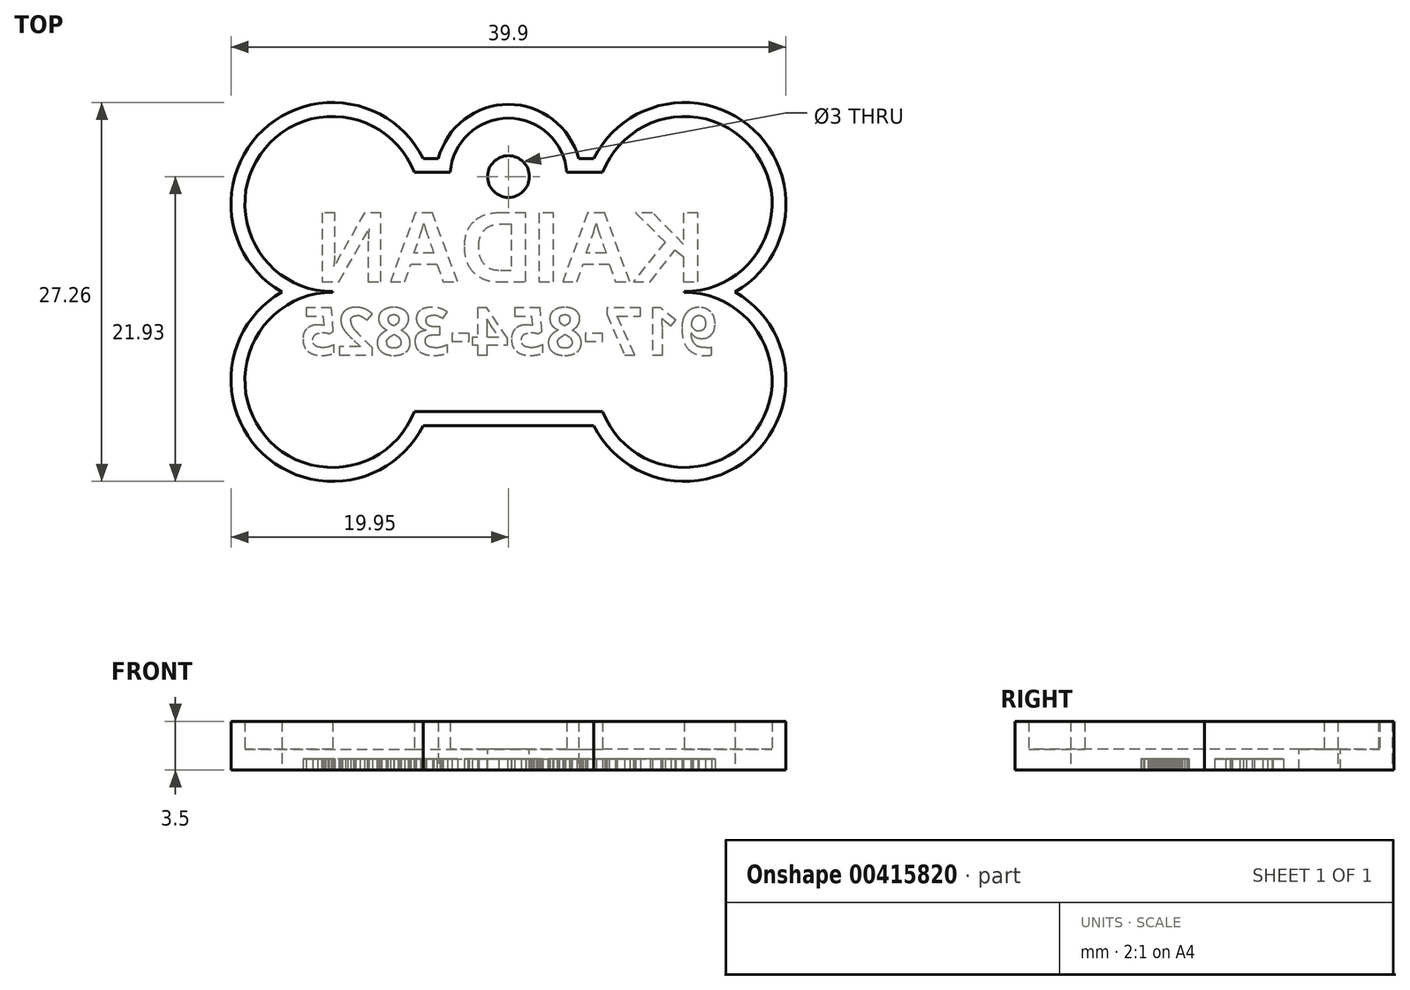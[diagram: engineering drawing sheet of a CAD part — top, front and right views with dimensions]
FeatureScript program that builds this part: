
annotation { "Feature Type Name" : "Feature", "Feature Type Description" : "" }
export const myFeature = defineFeature(function(context is Context, id is Id, definition is map)
    precondition{}
    {
        {
            var Q0;
            Q0=qCreatedBy(makeId("Top.planeOp"),FACE);
            var sketch = newSketch(context, id + "F0", { "sketchPlane" : qUnion([Q0])});
            skLineSegment(sketch, "E0.bottom", {"start": v(12.65, -6.32) * mm, "end": v(-12.65, -6.33) * mm, "construction": true});
            skLineSegment(sketch, "E0.top", {"start": v(12.65, 6.33) * mm, "end": v(-12.65, 6.32) * mm, "construction": true});
            skLineSegment(sketch, "E0.left", {"start": v(12.65, -6.32) * mm, "end": v(12.65, 6.33) * mm, "construction": true});
            skLineSegment(sketch, "E0.right", {"start": v(-12.65, -6.33) * mm, "end": v(-12.65, 6.32) * mm, "construction": true});
            skPoint(sketch, "E0.middle", {"position": v(0, 0) * mm});
            skArc(sketch, "E1", {"start": v(12.65, 0.03) * mm, "mid": v(17.85, 9.89) * mm, "end": v(6.78, 8.6) * mm});
            skArc(sketch, "E2", {"start": v(6.78, -8.6) * mm, "mid": v(17.85, -9.89) * mm, "end": v(12.65, -0.02) * mm});
            skArc(sketch, "E3", {"start": v(-12.65, -0.03) * mm, "mid": v(-17.85, -9.89) * mm, "end": v(-6.78, -8.6) * mm});
            skArc(sketch, "E4", {"start": v(-6.78, 8.6) * mm, "mid": v(-17.85, 9.89) * mm, "end": v(-12.65, 0.02) * mm});
            skLineSegment(sketch, "E5", {"start": v(-12.65, 0.02) * mm, "end": v(-12.65, -0.03) * mm});
            skLineSegment(sketch, "E6", {"start": v(12.65, -0.02) * mm, "end": v(12.65, 0.03) * mm});
            skLineSegment(sketch, "E7", {"start": v(-6.78, 8.6) * mm, "end": v(-4.19, 8.6) * mm});
            skLineSegment(sketch, "E8", {"start": v(-6.78, -8.6) * mm, "end": v(6.78, -8.6) * mm});
            skArc(sketch, "E9", {"start": v(4.19, 8.6) * mm, "mid": v(0, 12.5) * mm, "end": v(-4.19, 8.6) * mm});
            skPoint(sketch, "E10", {"position": v(0, 12.5) * mm});
            skCircle(sketch, "E11", {"center": v(0, 8.3) * mm, "radius": 1.5 * mm});
            skLineSegment(sketch, "E12.trimOffspring", {"start": v(4.19, 8.6) * mm, "end": v(6.78, 8.6) * mm});
            skLineSegment(sketch, "E13.0", {"start": v(-6.13, 9.6) * mm, "end": v(-5.03, 9.6) * mm});
            skArc(sketch, "E13.1", {"start": v(5.03, 9.6) * mm, "mid": v(0, 13.5) * mm, "end": v(-5.03, 9.6) * mm});
            skArc(sketch, "E13.2", {"start": v(-6.13, 9.6) * mm, "mid": v(-17.66, 11.63) * mm, "end": v(-16.3, 0) * mm});
            skLineSegment(sketch, "E13.3", {"start": v(5.03, 9.6) * mm, "end": v(6.13, 9.6) * mm});
            skArc(sketch, "E13.4", {"start": v(-16.3, 0) * mm, "mid": v(-17.66, -11.63) * mm, "end": v(-6.13, -9.6) * mm});
            skLineSegment(sketch, "E13.5", {"start": v(-6.13, -9.6) * mm, "end": v(6.13, -9.6) * mm});
            skArc(sketch, "E13.6", {"start": v(6.13, -9.6) * mm, "mid": v(17.66, -11.63) * mm, "end": v(16.3, 0) * mm});
            skArc(sketch, "E13.7", {"start": v(16.3, 0) * mm, "mid": v(17.66, 11.63) * mm, "end": v(6.13, 9.6) * mm});
            skSolve(sketch);
        }
        {
            var Q0;
            Q0=makeQuery(id+"F0.imprint","IMPRINT",FACE,{"disambiguationData":[TD([[makeQuery(id+"F0.imprint","IMPRINT",EDGE,{"derivedFrom":sQuery(id+"F0.wireOp",EDGE,"E1")}),-1.0]])]});
            extrude(context, id + "F1", {"entities" : qUnion([Q0]), "depth" : 2 * mm});
        }
        {
            var Q0;
            Q0=makeQuery(id+"F0.imprint","IMPRINT",FACE,{"disambiguationData":[TD([[makeQuery(id+"F0.imprint","IMPRINT",EDGE,{"derivedFrom":sQuery(id+"F0.wireOp",EDGE,"E1")}),1.0]])]});
            var Q1;
            Q1=makeQuery(id+"F0.imprint","IMPRINT",FACE,{"disambiguationData":[TD([[makeQuery(id+"F0.imprint","IMPRINT",EDGE,{"derivedFrom":sQuery(id+"F0.wireOp",EDGE,"E1")}),-1.0]])]});
            extrude(context, id + "F2", {"entities" : qUnion([Q0, Q1]), "operationType" : NewBodyOperationType.ADD, "oppositeDirection" : true, "depth" : 1.5 * mm});
        }
        {
            var Q0;
            Q0=makeQuery(id+"F2.opExtrude","CAP_FACE",FACE,{"disambiguationData":[OSD([sQuery(id+"F0.wireOp",EDGE,"E11"),sQuery(id+"F0.wireOp",EDGE,"E13.0"),sQuery(id+"F0.wireOp",EDGE,"E13.1"),sQuery(id+"F0.wireOp",EDGE,"E13.2"),sQuery(id+"F0.wireOp",EDGE,"E13.3"),sQuery(id+"F0.wireOp",EDGE,"E13.4"),sQuery(id+"F0.wireOp",EDGE,"E13.5"),sQuery(id+"F0.wireOp",EDGE,"E13.6"),sQuery(id+"F0.wireOp",EDGE,"E13.7")])],"isStart":false});
            var sketch = newSketch(context, id + "F3", { "sketchPlane" : qUnion([Q0])});
            skText(sketch, "E14", { "text": "KAIDAN", "fontName": "Arimo-Bold.ttf"});
            skText(sketch, "E15", { "text": "917-854-3825", "fontName": "OpenSans-Bold.ttf"});
            const initialGuessF3  = {"E14": [0.0141, -0.00074, -1, 0, 0.00518], "E15": [0.015, 0.00452, -1, 0, 0.0034]};
            skSetInitialGuess(sketch, initialGuessF3);
            skSolve(sketch);
        }
        {
            var Q0;
            Q0=makeQuery(id+"F3.imprint","IMPRINT",FACE,{"disambiguationData":[TD([[makeQuery(id+"F3.imprint","IMPRINT",EDGE,{"derivedFrom":sQuery(id+"F3.wireOp",EDGE,"E14.sketch_text.stroke-13")}),-1.0]])]});
            var Q1;
            Q1=makeQuery(id+"F3.imprint","IMPRINT",FACE,{"disambiguationData":[TD([[makeQuery(id+"F3.imprint","IMPRINT",EDGE,{"derivedFrom":sQuery(id+"F3.wireOp",EDGE,"E14.sketch_text.stroke-25")}),-1.0]])]});
            var Q2;
            Q2=makeQuery(id+"F3.imprint","IMPRINT",FACE,{"disambiguationData":[TD([[makeQuery(id+"F3.imprint","IMPRINT",EDGE,{"derivedFrom":sQuery(id+"F3.wireOp",EDGE,"E14.sketch_text.stroke-29")}),-1.0]])]});
            var Q3;
            Q3=makeQuery(id+"F3.imprint","IMPRINT",FACE,{"disambiguationData":[TD([[makeQuery(id+"F3.imprint","IMPRINT",EDGE,{"derivedFrom":sQuery(id+"F3.wireOp",EDGE,"E14.sketch_text.stroke-41")}),-1.0]])]});
            var Q4;
            Q4=makeQuery(id+"F3.imprint","IMPRINT",FACE,{"disambiguationData":[TD([[makeQuery(id+"F3.imprint","IMPRINT",EDGE,{"derivedFrom":sQuery(id+"F3.wireOp",EDGE,"E14.sketch_text.stroke-53")}),-1.0]])]});
            var Q5;
            Q5=makeQuery(id+"F3.imprint","IMPRINT",FACE,{"disambiguationData":[TD([[makeQuery(id+"F3.imprint","IMPRINT",EDGE,{"derivedFrom":sQuery(id+"F3.wireOp",EDGE,"E15.sketch_text.stroke-0")}),-1.0]])]});
            var Q6;
            Q6=makeQuery(id+"F3.imprint","IMPRINT",FACE,{"disambiguationData":[TD([[makeQuery(id+"F3.imprint","IMPRINT",EDGE,{"derivedFrom":sQuery(id+"F3.wireOp",EDGE,"E15.sketch_text.stroke-26")}),-1.0]])]});
            var Q7;
            Q7=makeQuery(id+"F3.imprint","IMPRINT",FACE,{"disambiguationData":[TD([[makeQuery(id+"F3.imprint","IMPRINT",EDGE,{"derivedFrom":sQuery(id+"F3.wireOp",EDGE,"E15.sketch_text.stroke-36")}),-1.0]])]});
            var Q8;
            Q8=makeQuery(id+"F3.imprint","IMPRINT",FACE,{"disambiguationData":[TD([[makeQuery(id+"F3.imprint","IMPRINT",EDGE,{"derivedFrom":sQuery(id+"F3.wireOp",EDGE,"E15.sketch_text.stroke-43")}),-1.0]])]});
            var Q9;
            Q9=makeQuery(id+"F3.imprint","IMPRINT",FACE,{"disambiguationData":[TD([[makeQuery(id+"F3.imprint","IMPRINT",EDGE,{"derivedFrom":sQuery(id+"F3.wireOp",EDGE,"E15.sketch_text.stroke-47")}),-1.0]])]});
            var Q10;
            Q10=makeQuery(id+"F3.imprint","IMPRINT",FACE,{"disambiguationData":[TD([[makeQuery(id+"F3.imprint","IMPRINT",EDGE,{"derivedFrom":sQuery(id+"F3.wireOp",EDGE,"E15.sketch_text.stroke-78")}),-1.0]])]});
            var Q11;
            Q11=makeQuery(id+"F3.imprint","IMPRINT",FACE,{"disambiguationData":[TD([[makeQuery(id+"F3.imprint","IMPRINT",EDGE,{"derivedFrom":sQuery(id+"F3.wireOp",EDGE,"E15.sketch_text.stroke-98")}),-1.0]])]});
            var Q12;
            Q12=makeQuery(id+"F3.imprint","IMPRINT",FACE,{"disambiguationData":[TD([[makeQuery(id+"F3.imprint","IMPRINT",EDGE,{"derivedFrom":sQuery(id+"F3.wireOp",EDGE,"E15.sketch_text.stroke-116")}),-1.0]])]});
            var Q13;
            Q13=makeQuery(id+"F3.imprint","IMPRINT",FACE,{"disambiguationData":[TD([[makeQuery(id+"F3.imprint","IMPRINT",EDGE,{"derivedFrom":sQuery(id+"F3.wireOp",EDGE,"E15.sketch_text.stroke-120")}),-1.0]])]});
            var Q14;
            Q14=makeQuery(id+"F3.imprint","IMPRINT",FACE,{"disambiguationData":[TD([[makeQuery(id+"F3.imprint","IMPRINT",EDGE,{"derivedFrom":sQuery(id+"F3.wireOp",EDGE,"E15.sketch_text.stroke-147")}),-1.0]])]});
            var Q15;
            Q15=makeQuery(id+"F3.imprint","IMPRINT",FACE,{"disambiguationData":[TD([[makeQuery(id+"F3.imprint","IMPRINT",EDGE,{"derivedFrom":sQuery(id+"F3.wireOp",EDGE,"E15.sketch_text.stroke-178")}),-1.0]])]});
            var Q16;
            Q16=makeQuery(id+"F3.imprint","IMPRINT",FACE,{"disambiguationData":[TD([[makeQuery(id+"F3.imprint","IMPRINT",EDGE,{"derivedFrom":sQuery(id+"F3.wireOp",EDGE,"E15.sketch_text.stroke-202")}),-1.0]])]});
            var Q17;
            Q17=makeQuery(id+"F3.imprint","IMPRINT",FACE,{"disambiguationData":[TD([[makeQuery(id+"F3.imprint","IMPRINT",EDGE,{"derivedFrom":sQuery(id+"F3.wireOp",EDGE,"E14.sketch_text.stroke-61")}),-1.0]])]});
            var Q18;
            Q18=makeQuery(id+"F3.imprint","IMPRINT",FACE,{"disambiguationData":[TD([[makeQuery(id+"F3.imprint","IMPRINT",EDGE,{"derivedFrom":sQuery(id+"F3.wireOp",EDGE,"E14.sketch_text.stroke-0")}),-1.0]])]});
            extrude(context, id + "F4", {"entities" : qUnion([Q0, Q1, Q2, Q3, Q4, Q5, Q6, Q7, Q8, Q9, Q10, Q11, Q12, Q13, Q14, Q15, Q16, Q17, Q18]), "operationType" : NewBodyOperationType.REMOVE, "oppositeDirection" : true, "depth" : .8 * mm});
        }
    });
